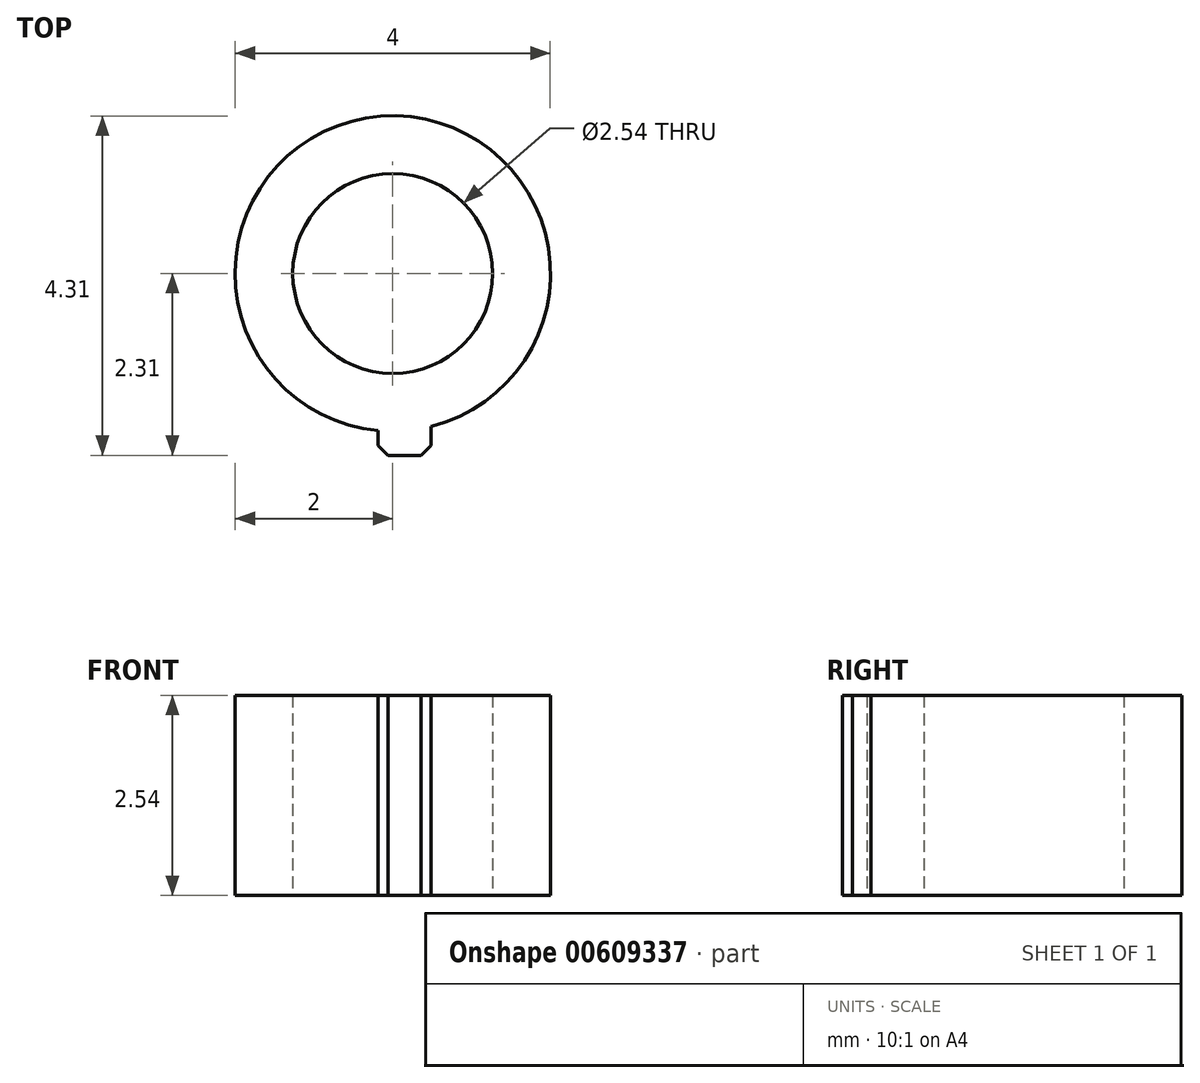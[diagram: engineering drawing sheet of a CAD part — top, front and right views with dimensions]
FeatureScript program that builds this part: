
annotation { "Feature Type Name" : "Feature", "Feature Type Description" : "" }
export const myFeature = defineFeature(function(context is Context, id is Id, definition is map)
    precondition{}
    {
        {
            var Q0;
            Q0=qCreatedBy(makeId("Top.planeOp"),FACE);
            var sketch = newSketch(context, id + "F0", { "sketchPlane" : qUnion([Q0])});
            skCircle(sketch, "E0", {"center": v(0, 0) * mm, "radius": 2 * mm});
            skCircle(sketch, "E1", {"center": v(0, 0) * mm, "radius": 1.27 * mm});
            skLineSegment(sketch, "E2.bottom", {"start": v(-0.19, -1.64) * mm, "end": v(0.49, -1.64) * mm});
            skLineSegment(sketch, "E2.top", {"start": v(-0.19, -2.31) * mm, "end": v(0.49, -2.31) * mm});
            skLineSegment(sketch, "E2.left", {"start": v(-0.19, -1.64) * mm, "end": v(-0.19, -2.31) * mm});
            skLineSegment(sketch, "E2.right", {"start": v(0.49, -1.64) * mm, "end": v(0.49, -2.31) * mm});
            skSolve(sketch);
        }
        {
            var Q0;
            Q0=makeQuery(id+"F0.imprint","IMPRINT",FACE,{"disambiguationData":[TD([[makeQuery(id+"F0.imprint","IMPRINT",EDGE,{"derivedFrom":sQuery(id+"F0.wireOp",EDGE,"E1")}),-1.0]])]});
            var Q1;
            {var subQ5=sQuery(id+"F0.wireOp",EDGE,"E2.bottom");Q1=makeQuery(id+"F0.imprint","IMPRINT",FACE,{"disambiguationData":[TD([[makeQuery(id+"F0.imprint","IMPRINT",EDGE,{"derivedFrom":subQ5}),-1.0]])]});}
            var Q2;
            {var subQ5=sQuery(id+"F0.wireOp",EDGE,"E2.top");Q2=makeQuery(id+"F0.imprint","IMPRINT",FACE,{"disambiguationData":[TD([[makeQuery(id+"F0.imprint","IMPRINT",EDGE,{"derivedFrom":subQ5}),1.0]])]});}
            extrude(context, id + "F1", {"entities" : qUnion([Q0, Q1, Q2]), "depth" : 2.54 * mm, "offsetDistance" : 25.4 * mm});
        }
        {
            var Q0;
            Q0=makeQuery(id+"F1.opExtrude","SWEPT_EDGE",EDGE,{"disambiguationData":[OSD([sQuery(id+"F0.wireOp",EDGE,"E2.top"),sQuery(id+"F0.wireOp",EDGE,"E2.left")])]});
            var Q1;
            Q1=makeQuery(id+"F1.opExtrude","SWEPT_EDGE",EDGE,{"disambiguationData":[OSD([sQuery(id+"F0.wireOp",EDGE,"E2.top"),sQuery(id+"F0.wireOp",EDGE,"E2.right")])]});
            chamfer(context, id + "F2", {"entities" : qUnion([Q0, Q1]), "width" : 0.13 * mm, "tangentPropagation" : true});
        }
    });
